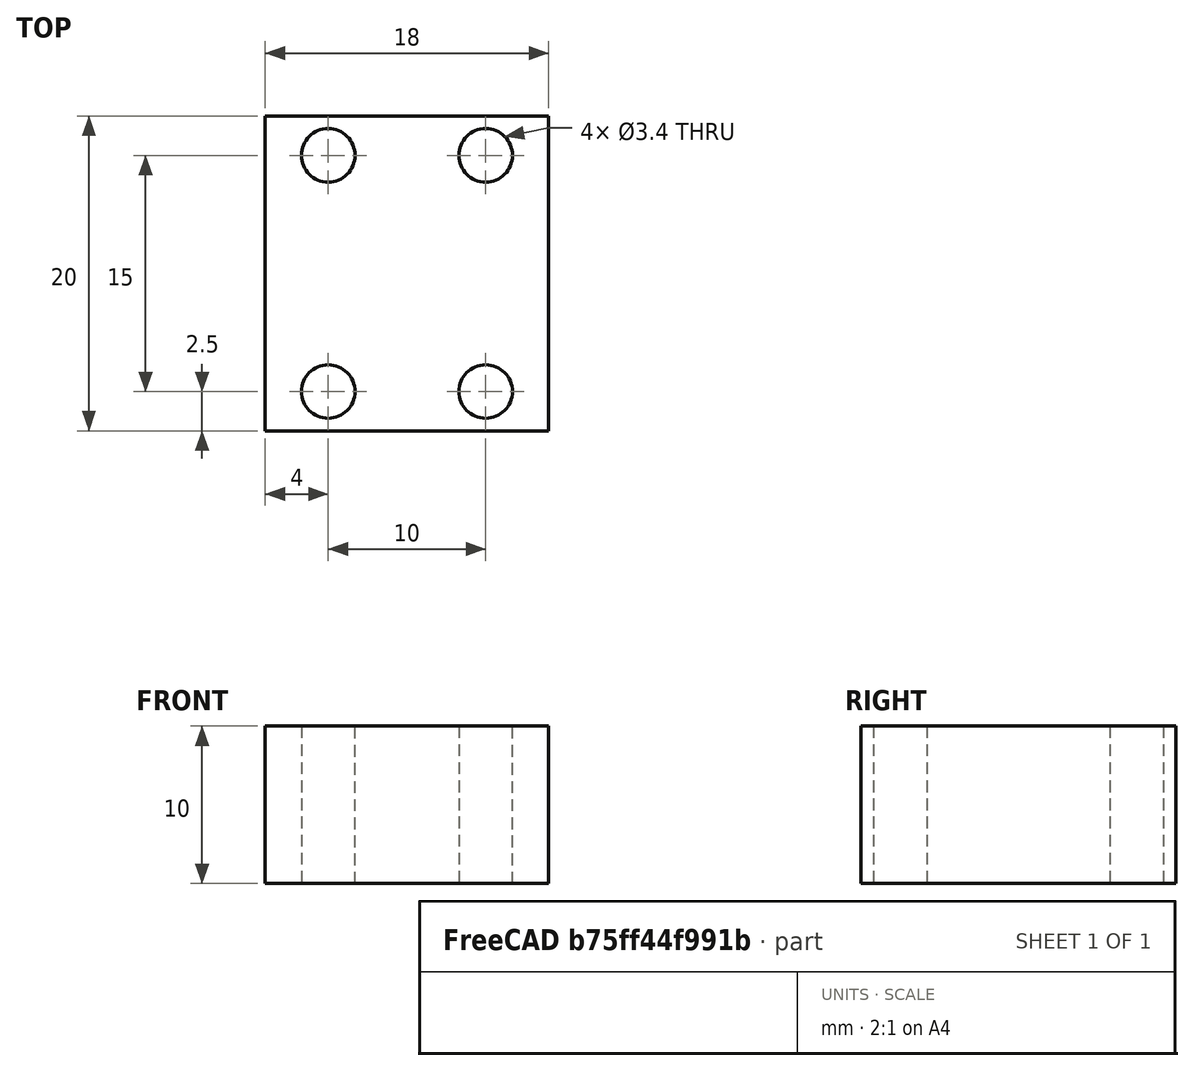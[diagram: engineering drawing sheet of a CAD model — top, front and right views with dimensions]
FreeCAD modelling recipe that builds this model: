
FCSTD DOCUMENT  (FreeCAD 0.18.4R)
Label: rehausseur_rail
License: All rights reserved
LicenseURL: http://en.wikipedia.org/wiki/All_rights_reserved
objects: Sketcher::SketchObject×1, PartDesign::Pad×1, PartDesign::Body×1
note: 4 computed .brp shape members not serialized (recipe doc carries the construction recipe); baked Part::Feature solids carry a one-line shape summary decoded from their .brp

FEATURE [Sketcher::SketchObject] Sketch
  MapMode = 5
  Support = -> [XY_Plane]
  sketch-geometry (8):
    g0: LineSegment StartX=-9 StartY=-10 StartZ=0 EndX=9 EndY=-10 EndZ=0
    g1: LineSegment StartX=9 StartY=-10 StartZ=0 EndX=9 EndY=10 EndZ=0
    g2: LineSegment StartX=9 StartY=10 StartZ=0 EndX=-9 EndY=10 EndZ=0
    g3: LineSegment StartX=-9 StartY=10 StartZ=0 EndX=-9 EndY=-10 EndZ=0
    g4: Circle CenterX=-5 CenterY=7.5 CenterZ=0 NormalX=0 NormalY=0 NormalZ=1 AngleXU=0 Radius=1.7
    g5: Circle CenterX=-5 CenterY=-7.5 CenterZ=0 NormalX=0 NormalY=0 NormalZ=1 AngleXU=0 Radius=1.7
    g6: Circle CenterX=5 CenterY=7.5 CenterZ=0 NormalX=0 NormalY=0 NormalZ=1 AngleXU=0 Radius=1.7
    g7: Circle CenterX=5 CenterY=-7.5 CenterZ=0 NormalX=0 NormalY=0 NormalZ=1 AngleXU=0 Radius=1.7
  constraints (19):
    c: Coincident(g0,g1)
    c: Coincident(g1,g2)
    c: Coincident(g2,g3)
    c: Coincident(g3,g0)
    c: Horizontal(g0)
    c: Vertical(g1)
    c: DistanceX(g2,g2) = 18
    c: DistanceY(g3,g3) = 20
    c: Symmetric(g2,g1,g-2)
    c: Symmetric(g2,g0,g-1)
    c: Radius(g6) = 1.7
    c: Radius(g4) = 1.7
    c: Radius(g5) = 1.7
    c: Radius(g7) = 1.7
    c: Distance(g6,g4) = 10
    c: Distance(g5,g4) = 15
    c: Symmetric(g4,g6,g-2)
    c: Symmetric(g5,g7,g-2)
    c: Symmetric(g5,g4,g-1)
FEATURE [PartDesign::Pad] Pad
  Length = 10
  Length2 = 100
  Profile = -> Sketch
  Type = 0
FEATURE [PartDesign::Body] Body
  Group = -> [Sketch,Pad]
  Origin = -> Origin
  Tip = -> Pad
